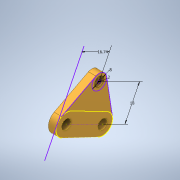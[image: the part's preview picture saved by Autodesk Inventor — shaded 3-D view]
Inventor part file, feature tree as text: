
AUTODESK INVENTOR PART (.ipt)
format: ipt  version: 2020 (Build 240168000, 168)  size: 150,528 bytes
history: native  units: in
note: dims shown in document units (in); Inventor stores cm internally (conversion verified against a paired STEP export)
features: extrude x3, sketch x3, projected_geometry x1
ambient origin geometry x8: Origin, YZ Plane, XZ Plane, XY Plane, X Axis, Y Axis, Z Axis, Center Point
bodies: Solid1 (feature_tree)
feature tree (7):
  extrude  "Extrusion1"  Depth=0.4523in
  extrude  "Extrusion2"  Depth=0.2118in
  extrude  "Extrusion3"  Depth=0.1575in TaperAngle=0.0deg
  sketch  "Sketch1"  dims[d0=0.2008in d1=0.2008in d3=0.4523in]
  sketch  "Sketch2"  dims[d4=0.2118in d5=0.8586in]
  projected_geometry  "Projected Loop1"
  sketch  "Sketch3"  dims[d6=0.8656in d7=0.1575in d8=0.0in d11=0.0787in d12=0.315in d13=0.1575in d14=0.0in d15=0.1969in d16=0.0787in d17=0.0in d18=0.6591in d19=0.7087in]
